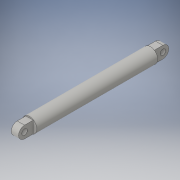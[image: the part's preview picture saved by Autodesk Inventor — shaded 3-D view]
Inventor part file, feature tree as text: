
AUTODESK INVENTOR PART (.ipt)
format: ipt  version: 2016 (Build 200138000, 138)  size: 118,784 bytes
history: native  units: in
note: dims shown in document units (in); Inventor stores cm internally (conversion verified against a paired STEP export)
features: extrude x3, sketch x3, fillet x1, mirror x1
ambient origin geometry x8: Origin, YZ Plane, XZ Plane, XY Plane, X Axis, Y Axis, Z Axis, Center Point
bodies: Solid1 (feature_tree)
feature tree (8):
  extrude  "Extrusion1"  Depth=16.5in TaperAngle=0.0deg
  extrude  "Extrusion4"  Depth=0.8125in
  fillet  "Fillet2"  Radius=2.0in
  extrude  "Extrusion5"  Depth=1.625in
  mirror  "Mirror1"
  sketch  "Sketch1"  dims[d0=2.0in d1=16.5in d2=0.0in]
  sketch  "Sketch4"  dims[d10=2.0in d11=0.0in d12=0.8125in d13=2.0in d14=0.0in]
  sketch  "Sketch5"  dims[d15=1.0in d16=1.625in]
